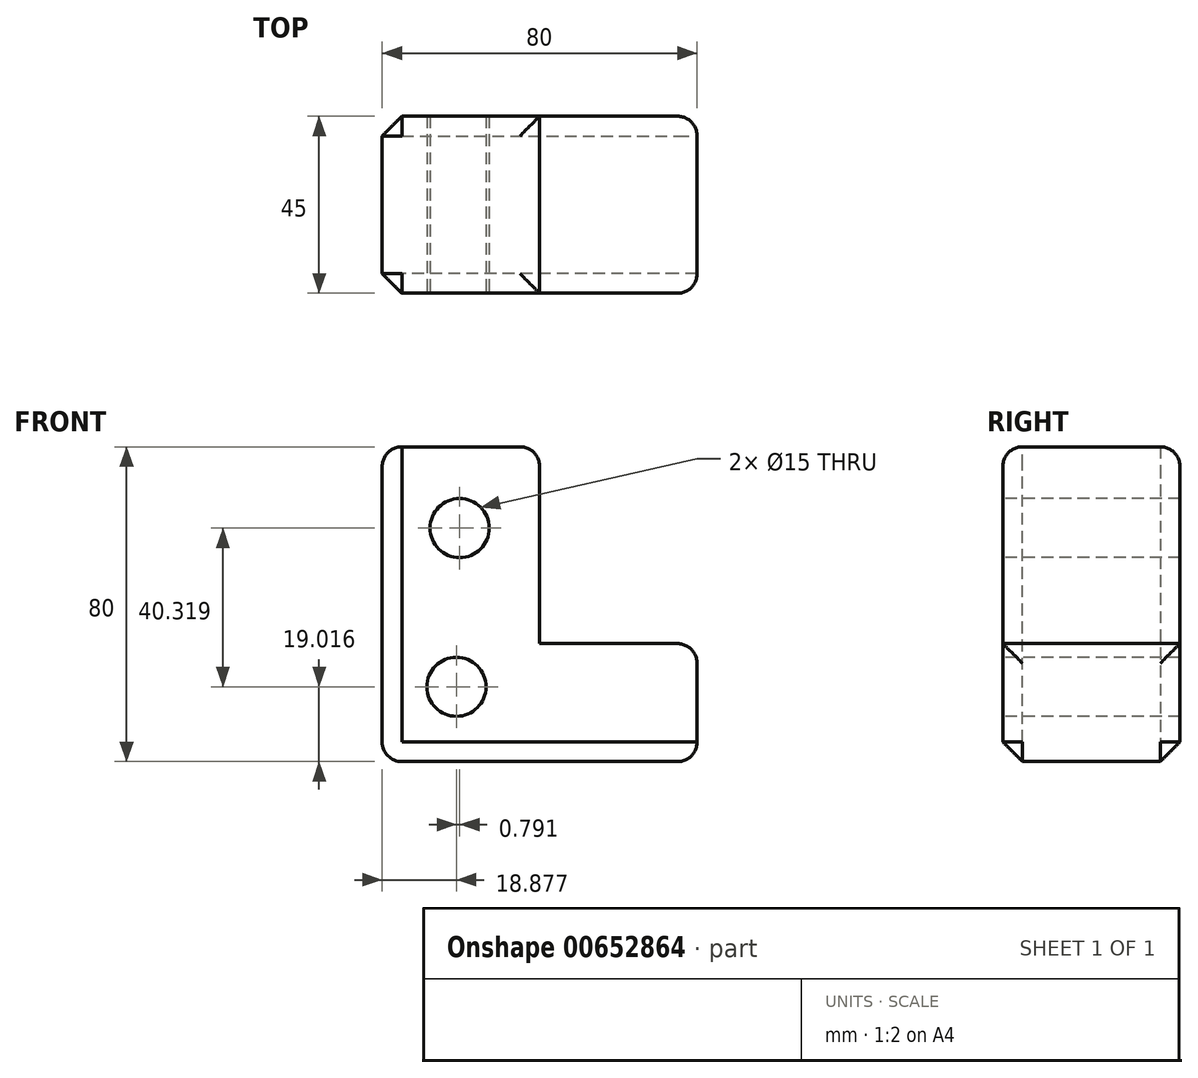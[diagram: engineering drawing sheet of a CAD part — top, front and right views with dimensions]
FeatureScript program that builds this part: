
annotation { "Feature Type Name" : "Feature", "Feature Type Description" : "" }
export const myFeature = defineFeature(function(context is Context, id is Id, definition is map)
    precondition{}
    {
        {
            var Q0;
            Q0=qCreatedBy(makeId("Front.planeOp"),FACE);
            var sketch = newSketch(context, id + "F0", { "sketchPlane" : qUnion([Q0])});
            skLineSegment(sketch, "E0.bottom", {"start": v(0, 0) * mm, "end": v(-40, 0) * mm});
            skLineSegment(sketch, "E0.top", {"start": v(0, 80) * mm, "end": v(-40, 80) * mm});
            skLineSegment(sketch, "E0.left", {"start": v(0, 0) * mm, "end": v(0, 80) * mm});
            skLineSegment(sketch, "E0.right", {"start": v(-40, 0) * mm, "end": v(-40, 80) * mm});
            skLineSegment(sketch, "E1.bottom", {"start": v(0, 0) * mm, "end": v(40, 0) * mm});
            skLineSegment(sketch, "E1.top", {"start": v(0, 30) * mm, "end": v(40, 30) * mm});
            skLineSegment(sketch, "E1.left", {"start": v(0, 0) * mm, "end": v(0, 30) * mm});
            skLineSegment(sketch, "E1.right", {"start": v(40, 0) * mm, "end": v(40, 30) * mm});
            skSolve(sketch);
        }
        {
            var Q0;
            Q0=makeQuery(id+"F0.imprint","IMPRINT",FACE,{"disambiguationData":[TD([[makeQuery(id+"F0.imprint","IMPRINT",EDGE,{"derivedFrom":sQuery(id+"F0.wireOp",EDGE,"E0.bottom")}),-1.0]])]});
            var sketch = newSketch(context, id + "F1", { "sketchPlane" : qUnion([Q0])});
            skCircle(sketch, "E2", {"center": v(-20.33, 59.34) * mm, "radius": 7.5 * mm});
            skCircle(sketch, "E3", {"center": v(-21.12, 19.02) * mm, "radius": 7.5 * mm});
            skSolve(sketch);
        }
        {
            var Q0;
            Q0 = qSketchRegion(id + "F0", true);
            extrude(context, id + "F2", {"entities" : qUnion([Q0]), "depth" : 45 * mm, "offsetDistance" : 25 * mm});
        }
        {
            var Q0;
            Q0=makeQuery(id+"F2.opExtrude","SWEPT_EDGE",EDGE,{"disambiguationData":[OSD([sQuery(id+"F0.wireOp",EDGE,"E0.top"),sQuery(id+"F0.wireOp",EDGE,"E0.left")])]});
            var Q1;
            Q1=makeQuery(id+"F2.opExtrude","CAP_EDGE",EDGE,{"disambiguationData":[OSD([sQuery(id+"F0.wireOp",EDGE,"E0.top")])],"isStart":false});
            var Q2;
            Q2=makeQuery(id+"F2.opExtrude","SWEPT_EDGE",EDGE,{"disambiguationData":[OSD([sQuery(id+"F0.wireOp",EDGE,"E0.top"),sQuery(id+"F0.wireOp",EDGE,"E0.right")])]});
            var Q3;
            Q3=makeQuery(id+"F2.opExtrude","CAP_EDGE",EDGE,{"disambiguationData":[OSD([sQuery(id+"F0.wireOp",EDGE,"E0.top")])],"isStart":true});
            var Q4;
            Q4=makeQuery(id+"F2.opExtrude","CAP_EDGE",EDGE,{"disambiguationData":[OSD([sQuery(id+"F0.wireOp",EDGE,"E1.right")])],"isStart":true});
            var Q5;
            Q5=makeQuery(id+"F2.opExtrude","SWEPT_EDGE",EDGE,{"disambiguationData":[OSD([sQuery(id+"F0.wireOp",EDGE,"E1.bottom"),sQuery(id+"F0.wireOp",EDGE,"E1.right")])]});
            var Q6;
            Q6=makeQuery(id+"F2.opExtrude","CAP_EDGE",EDGE,{"disambiguationData":[OSD([sQuery(id+"F0.wireOp",EDGE,"E1.right")])],"isStart":false});
            var Q7;
            Q7=makeQuery(id+"F2.opExtrude","SWEPT_EDGE",EDGE,{"disambiguationData":[OSD([sQuery(id+"F0.wireOp",EDGE,"E1.top"),sQuery(id+"F0.wireOp",EDGE,"E1.right")])]});
            var Q8;
            Q8=makeQuery(id+"F2.opExtrude","SWEPT_EDGE",EDGE,{"disambiguationData":[OSD([sQuery(id+"F0.wireOp",EDGE,"E0.bottom"),sQuery(id+"F0.wireOp",EDGE,"E0.right")])]});
            fillet(context, id + "F3", {"entities" : qUnion([Q0, Q1, Q2, Q3, Q4, Q5, Q6, Q7, Q8]), "radius" : 5 * mm, "tangentPropagation" : true, "allowEdgeOverflow" : false});
        }
        {
            var Q0;
            Q0=makeQuery(id+"F2.opExtrude","CAP_EDGE",EDGE,{"disambiguationData":[OSD([sQuery(id+"F0.wireOp",EDGE,"E0.right")])],"isStart":false});
            var Q1;
            Q1=makeQuery(id+"F2.opExtrude","CAP_EDGE",EDGE,{"disambiguationData":[OSD([sQuery(id+"F0.wireOp",EDGE,"E0.right")])],"isStart":true});
            chamfer(context, id + "F4", {"entities" : qUnion([Q0, Q1]), "width" : 5 * mm, "tangentPropagation" : true});
        }
        {
            var Q0;
            Q0=makeQuery(id+"F1.imprint","IMPRINT",FACE,{"disambiguationData":[TD([[makeQuery(id+"F1.imprint","IMPRINT",EDGE,{"derivedFrom":sQuery(id+"F1.wireOp",EDGE,"E2")}),1.0]])]});
            var Q1;
            Q1=makeQuery(id+"F1.imprint","IMPRINT",FACE,{"disambiguationData":[TD([[makeQuery(id+"F1.imprint","IMPRINT",EDGE,{"derivedFrom":sQuery(id+"F1.wireOp",EDGE,"E3")}),1.0]])]});
            extrude(context, id + "F5", {"entities" : qUnion([Q0, Q1]), "operationType" : NewBodyOperationType.REMOVE, "endBound" : BoundingType.SYMMETRIC, "oppositeDirection" : true, "depth" : 664 * mm, "offsetDistance" : 25 * mm});
        }
    });
